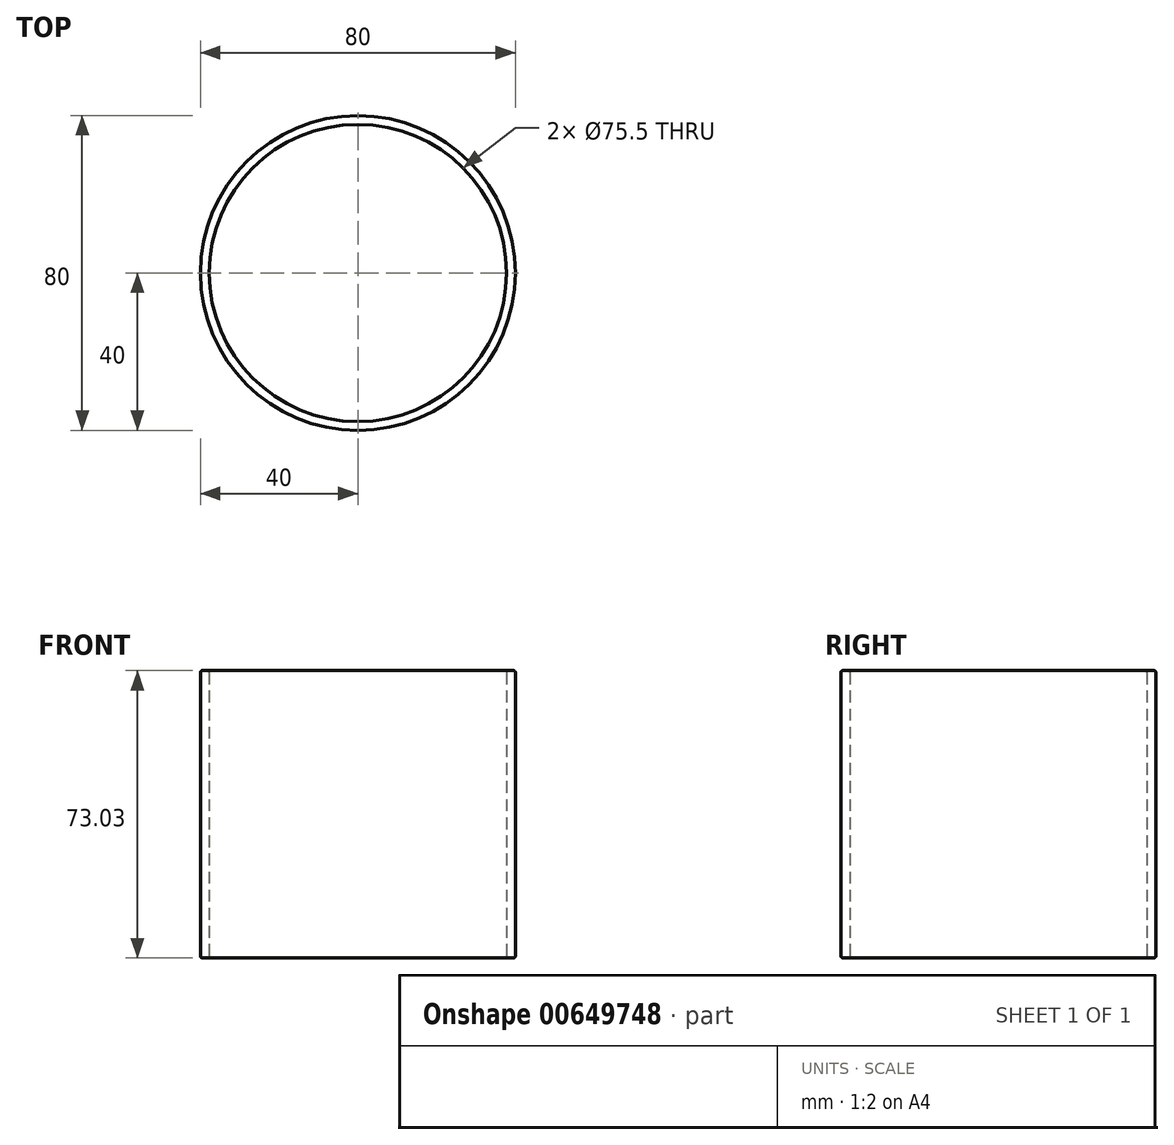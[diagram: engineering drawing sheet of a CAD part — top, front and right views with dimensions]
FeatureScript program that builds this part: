
annotation { "Feature Type Name" : "Feature", "Feature Type Description" : "" }
export const myFeature = defineFeature(function(context is Context, id is Id, definition is map)
    precondition{}
    {
        {
            var Q0;
            Q0=qCreatedBy(makeId("Top.planeOp"),FACE);
            var sketch = newSketch(context, id + "F0", { "sketchPlane" : qUnion([Q0])});
            skCircle(sketch, "E0", {"center": v(0, 0) * mm, "radius": 40 * mm});
            skCircle(sketch, "E1", {"center": v(0, 0) * mm, "radius": 37.75 * mm});
            skSolve(sketch);
        }
        {
            var Q0;
            Q0=qSketchRegion(id+"F0",true);
            extrude(context, id + "F1", {"entities" : qUnion([Q0]), "depth" : 73.02 * mm, "offsetDistance" : 25.4 * mm});
        }
        {
            var Q0;
            Q0=makeQuery(id+"F1.opExtrude","CAP_EDGE",EDGE,{"disambiguationData":[OSD([sQuery(id+"F0.wireOp",EDGE,"E0")])],"isStart":false});
            var Q1;
            Q1=makeQuery(id+"F1.opExtrude","CAP_EDGE",EDGE,{"disambiguationData":[OSD([sQuery(id+"F0.wireOp",EDGE,"E1")])],"isStart":false});
            var Q2;
            Q2=makeQuery(id+"F1.opExtrude","CAP_EDGE",EDGE,{"disambiguationData":[OSD([sQuery(id+"F0.wireOp",EDGE,"E0")])],"isStart":true});
            var Q3;
            Q3=makeQuery(id+"F1.opExtrude","CAP_EDGE",EDGE,{"disambiguationData":[OSD([sQuery(id+"F0.wireOp",EDGE,"E1")])],"isStart":true});
            fillet(context, id + "F2", {"entities" : qUnion([Q0, Q1, Q2, Q3]), "radius" : .5 * mm, "tangentPropagation" : true, "allowEdgeOverflow" : false});
        }
    });
